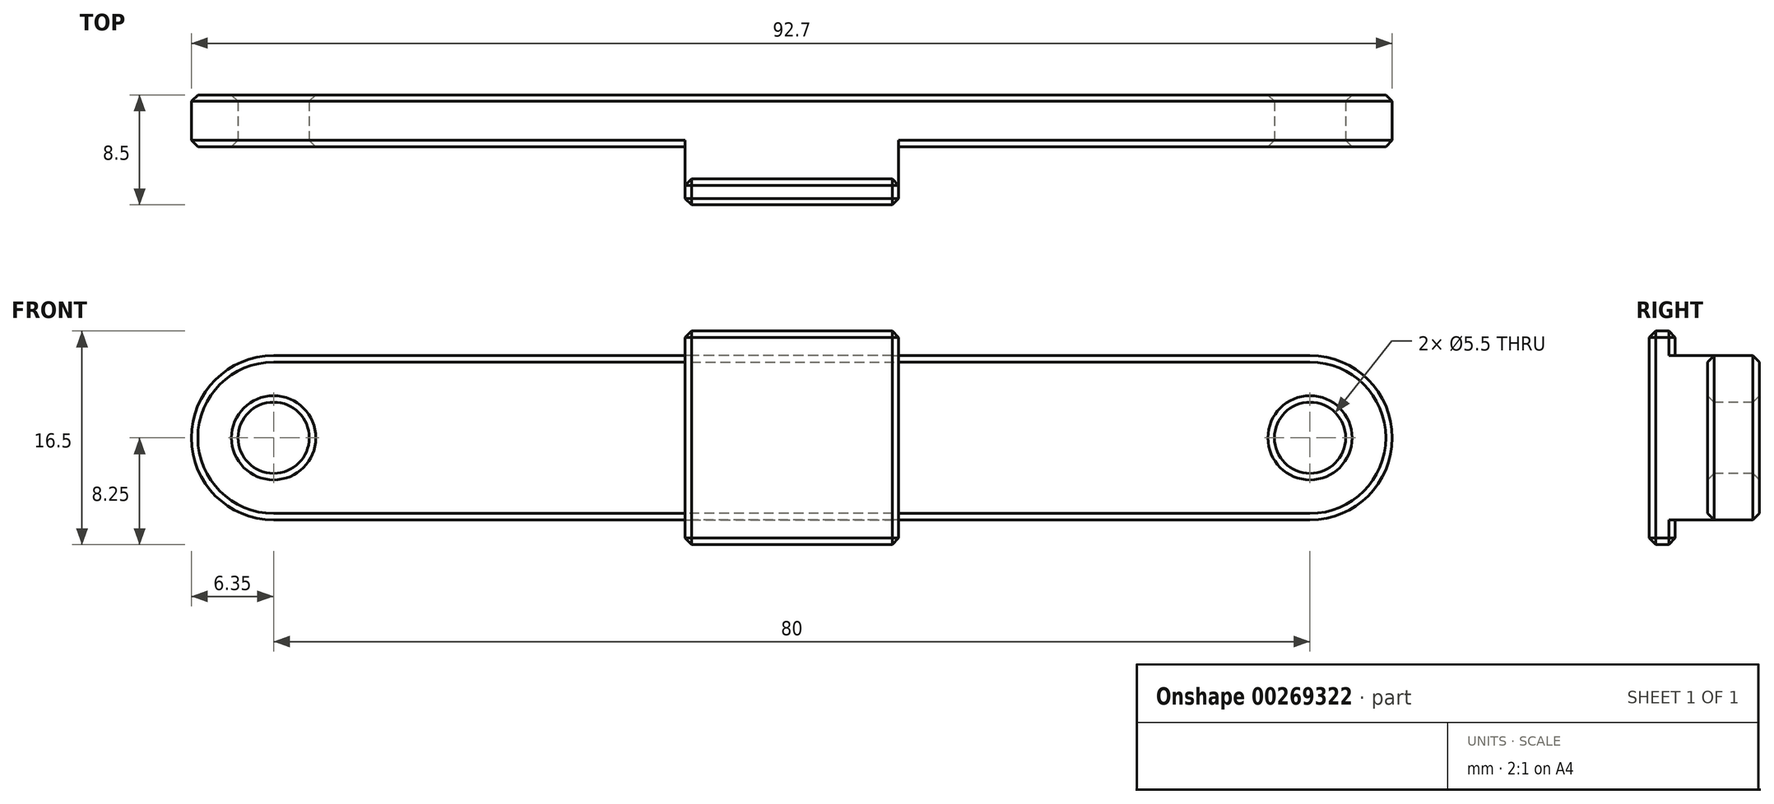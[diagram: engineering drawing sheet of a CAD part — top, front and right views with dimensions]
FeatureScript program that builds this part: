
annotation { "Feature Type Name" : "Feature", "Feature Type Description" : "" }
export const myFeature = defineFeature(function(context is Context, id is Id, definition is map)
    precondition{}
    {
        {
            var Q0;
            Q0=qCreatedBy(makeId("Front.planeOp"),FACE);
            var sketch = newSketch(context, id + "F0", { "sketchPlane" : qUnion([Q0])});
            skLineSegment(sketch, "E0.bottom", {"start": v(40, 6.35) * mm, "end": v(-40, 6.35) * mm});
            skLineSegment(sketch, "E0.top", {"start": v(40, -6.35) * mm, "end": v(-40, -6.35) * mm});
            skPoint(sketch, "E0.middle", {"position": v(0, 0) * mm});
            skArc(sketch, "E1", {"start": v(-40, 6.35) * mm, "mid": v(-46.35, 0) * mm, "end": v(-40, -6.35) * mm});
            skArc(sketch, "E2", {"start": v(40, -6.35) * mm, "mid": v(46.35, 0) * mm, "end": v(40, 6.35) * mm});
            skCircle(sketch, "E3", {"center": v(-40, 0) * mm, "radius": 2.75 * mm});
            skCircle(sketch, "E4", {"center": v(40, 0) * mm, "radius": 2.75 * mm});
            skSolve(sketch);
        }
        {
            var Q0;
            Q0=qSketchRegion(id+"F0",true);
            extrude(context, id + "F1", {"entities" : qUnion([Q0]), "oppositeDirection" : true, "depth" : 4 * mm});
        }
        {
            var Q0;
            Q0=qCreatedBy(makeId("Front.planeOp"),FACE);
            var sketch = newSketch(context, id + "F2", { "sketchPlane" : qUnion([Q0])});
            skLineSegment(sketch, "E5.bottom", {"start": v(8.25, 8.25) * mm, "end": v(-8.25, 8.25) * mm});
            skLineSegment(sketch, "E5.top", {"start": v(8.25, -8.25) * mm, "end": v(-8.25, -8.25) * mm});
            skLineSegment(sketch, "E5.left", {"start": v(8.25, 8.25) * mm, "end": v(8.25, -8.25) * mm});
            skLineSegment(sketch, "E5.right", {"start": v(-8.25, 8.25) * mm, "end": v(-8.25, -8.25) * mm});
            skPoint(sketch, "E5.middle", {"position": v(0, 0) * mm});
            skSolve(sketch);
        }
        {
            var Q0;
            Q0=makeQuery(id+"F2.imprint","IMPRINT",FACE,{"disambiguationData":[TD([[makeQuery(id+"F2.imprint","IMPRINT",EDGE,{"derivedFrom":sQuery(id+"F2.wireOp",EDGE,"E5.bottom")}),1.0]])]});
            extrude(context, id + "F3", {"entities" : qUnion([Q0]), "operationType" : NewBodyOperationType.ADD, "depth" : 4.5 * mm});
        }
        {
            var Q0;
            Q0=makeQuery(id+"F1.opExtrude","CAP_FACE",FACE,{"disambiguationData":[OSD([sQuery(id+"F0.wireOp",EDGE,"E0.bottom"),sQuery(id+"F0.wireOp",EDGE,"E0.top"),sQuery(id+"F0.wireOp",EDGE,"E1"),sQuery(id+"F0.wireOp",EDGE,"E2"),sQuery(id+"F0.wireOp",EDGE,"E3"),sQuery(id+"F0.wireOp",EDGE,"E4")])],"isStart":true});
            var sketch = newSketch(context, id + "F4", { "sketchPlane" : qUnion([Q0])});
            skLineSegment(sketch, "E6.bottom", {"start": v(8.25, -6.35) * mm, "end": v(-8.25, -6.35) * mm});
            skLineSegment(sketch, "E6.top", {"start": v(8.25, 6.35) * mm, "end": v(-8.25, 6.35) * mm});
            skLineSegment(sketch, "E6.left", {"start": v(8.25, -6.35) * mm, "end": v(8.25, 6.35) * mm});
            skLineSegment(sketch, "E6.right", {"start": v(-8.25, -6.35) * mm, "end": v(-8.25, 6.35) * mm});
            skPoint(sketch, "E6.middle", {"position": v(0, 0) * mm});
            skLineSegment(sketch, "E7.0", {"start": v(13.25, 11.35) * mm, "end": v(-13.25, 11.35) * mm});
            skLineSegment(sketch, "E7.1", {"start": v(13.25, -11.35) * mm, "end": v(13.25, 11.35) * mm});
            skLineSegment(sketch, "E7.2", {"start": v(13.25, -11.35) * mm, "end": v(-13.25, -11.35) * mm});
            skLineSegment(sketch, "E7.3", {"start": v(-13.25, -11.35) * mm, "end": v(-13.25, 11.35) * mm});
            skSolve(sketch);
        }
        {
            var Q0;
            Q0=qSketchRegion(id+"F4",true);
            extrude(context, id + "F5", {"entities" : qUnion([Q0]), "operationType" : NewBodyOperationType.REMOVE, "depth" : 2.5 * mm});
        }
        {
            var Q0;
            {var subQ0=sQuery(id+"F0.wireOp",EDGE,"E3");var subQ1=sQuery(id+"F0.wireOp",EDGE,"E1");var subQ3=sQuery(id+"F0.wireOp",EDGE,"E0.top");var subQ4=sQuery(id+"F0.wireOp",EDGE,"E0.bottom");Q0=makeQuery(id+"F3.boolean.opBoolean","SPLIT",FACE,{"disambiguationData":[TD([makeQuery(id+"F1.opExtrude","SWEPT_FACE",FACE,{"disambiguationData":[OSD([subQ1])]})])],"derivedFrom":makeQuery(id+"F1.opExtrude","CAP_FACE",FACE,{"disambiguationData":[OSD([subQ4,subQ3,subQ1,sQuery(id+"F0.wireOp",EDGE,"E2"),subQ0,sQuery(id+"F0.wireOp",EDGE,"E4")])],"isStart":true})});}
            var sketch = newSketch(context, id + "F6", { "sketchPlane" : qUnion([Q0])});
            skCircle(sketch, "E8", {"center": v(-25, 0) * mm, "radius": 2.75 * mm});
            skCircle(sketch, "E9", {"center": v(25, 0) * mm, "radius": 2.75 * mm});
            skSolve(sketch);
        }
        {
            var Q0;
            Q0=makeQuery(id+"F3.opExtrude","CAP_FACE",FACE,{"disambiguationData":[OSD([sQuery(id+"F2.wireOp",EDGE,"E5.bottom"),sQuery(id+"F2.wireOp",EDGE,"E5.top"),sQuery(id+"F2.wireOp",EDGE,"E5.left"),sQuery(id+"F2.wireOp",EDGE,"E5.right")])],"isStart":false});
            var Q1;
            Q1=makeQuery(id+"F3.opExtrude","SWEPT_EDGE",EDGE,{"disambiguationData":[OSD([sQuery(id+"F2.wireOp",EDGE,"E5.bottom"),sQuery(id+"F2.wireOp",EDGE,"E5.left")])]});
            var Q2;
            Q2=makeQuery(id+"F3.opExtrude","SWEPT_EDGE",EDGE,{"disambiguationData":[OSD([sQuery(id+"F2.wireOp",EDGE,"E5.bottom"),sQuery(id+"F2.wireOp",EDGE,"E5.right")])]});
            var Q3;
            Q3=makeQuery(id+"F3.opExtrude","SWEPT_EDGE",EDGE,{"disambiguationData":[OSD([sQuery(id+"F2.wireOp",EDGE,"E5.top"),sQuery(id+"F2.wireOp",EDGE,"E5.right")])]});
            var Q4;
            Q4=makeQuery(id+"F3.opExtrude","SWEPT_EDGE",EDGE,{"disambiguationData":[OSD([sQuery(id+"F2.wireOp",EDGE,"E5.top"),sQuery(id+"F2.wireOp",EDGE,"E5.left")])]});
            var Q5;
            Q5=makeQuery(id+"F1.opExtrude","CAP_FACE",FACE,{"disambiguationData":[OSD([sQuery(id+"F0.wireOp",EDGE,"E0.bottom"),sQuery(id+"F0.wireOp",EDGE,"E0.top"),sQuery(id+"F0.wireOp",EDGE,"E1"),sQuery(id+"F0.wireOp",EDGE,"E2"),sQuery(id+"F0.wireOp",EDGE,"E3"),sQuery(id+"F0.wireOp",EDGE,"E4")])],"isStart":false});
            var Q6;
            Q6=makeQuery(id+"F5.boolean.opBoolean","INTERSECT",EDGE,{"derivedFrom":[makeQuery(id+"F3.opExtrude","SWEPT_FACE",FACE,{"disambiguationData":[OSD([sQuery(id+"F2.wireOp",EDGE,"E5.bottom")])]}),makeQuery(id+"F5.opExtrude","CAP_FACE",FACE,{"disambiguationData":[OSD([sQuery(id+"F4.wireOp",EDGE,"E6.bottom"),sQuery(id+"F4.wireOp",EDGE,"E6.top"),sQuery(id+"F4.wireOp",EDGE,"E6.left"),sQuery(id+"F4.wireOp",EDGE,"E6.right"),sQuery(id+"F4.wireOp",EDGE,"E7.0"),sQuery(id+"F4.wireOp",EDGE,"E7.1"),sQuery(id+"F4.wireOp",EDGE,"E7.2"),sQuery(id+"F4.wireOp",EDGE,"E7.3")])],"isStart":false})]});
            var Q7;
            Q7=makeQuery(id+"F5.boolean.opBoolean","INTERSECT",EDGE,{"derivedFrom":[makeQuery(id+"F3.opExtrude","SWEPT_FACE",FACE,{"disambiguationData":[OSD([sQuery(id+"F2.wireOp",EDGE,"E5.left")])]}),makeQuery(id+"F5.opExtrude","CAP_FACE",FACE,{"disambiguationData":[OSD([sQuery(id+"F4.wireOp",EDGE,"E6.bottom"),sQuery(id+"F4.wireOp",EDGE,"E6.top"),sQuery(id+"F4.wireOp",EDGE,"E6.left"),sQuery(id+"F4.wireOp",EDGE,"E6.right"),sQuery(id+"F4.wireOp",EDGE,"E7.0"),sQuery(id+"F4.wireOp",EDGE,"E7.1"),sQuery(id+"F4.wireOp",EDGE,"E7.2"),sQuery(id+"F4.wireOp",EDGE,"E7.3")])],"isStart":false})]});
            var Q8;
            Q8=makeQuery(id+"F5.boolean.opBoolean","INTERSECT",EDGE,{"derivedFrom":[makeQuery(id+"F3.opExtrude","SWEPT_FACE",FACE,{"disambiguationData":[OSD([sQuery(id+"F2.wireOp",EDGE,"E5.right")])]}),makeQuery(id+"F5.opExtrude","CAP_FACE",FACE,{"disambiguationData":[OSD([sQuery(id+"F4.wireOp",EDGE,"E6.bottom"),sQuery(id+"F4.wireOp",EDGE,"E6.top"),sQuery(id+"F4.wireOp",EDGE,"E6.left"),sQuery(id+"F4.wireOp",EDGE,"E6.right"),sQuery(id+"F4.wireOp",EDGE,"E7.0"),sQuery(id+"F4.wireOp",EDGE,"E7.1"),sQuery(id+"F4.wireOp",EDGE,"E7.2"),sQuery(id+"F4.wireOp",EDGE,"E7.3")])],"isStart":false})]});
            var Q9;
            Q9=makeQuery(id+"F5.boolean.opBoolean","INTERSECT",EDGE,{"derivedFrom":[makeQuery(id+"F3.opExtrude","SWEPT_FACE",FACE,{"disambiguationData":[OSD([sQuery(id+"F2.wireOp",EDGE,"E5.top")])]}),makeQuery(id+"F5.opExtrude","CAP_FACE",FACE,{"disambiguationData":[OSD([sQuery(id+"F4.wireOp",EDGE,"E6.bottom"),sQuery(id+"F4.wireOp",EDGE,"E6.top"),sQuery(id+"F4.wireOp",EDGE,"E6.left"),sQuery(id+"F4.wireOp",EDGE,"E6.right"),sQuery(id+"F4.wireOp",EDGE,"E7.0"),sQuery(id+"F4.wireOp",EDGE,"E7.1"),sQuery(id+"F4.wireOp",EDGE,"E7.2"),sQuery(id+"F4.wireOp",EDGE,"E7.3")])],"isStart":false})]});
            var Q10;
            {var subQ0=sQuery(id+"F2.wireOp",EDGE,"E5.left");var subQ1=makeQuery(id+"F3.opExtrude","SWEPT_FACE",FACE,{"disambiguationData":[OSD([subQ0])]});var subQ2=sQuery(id+"F2.wireOp",EDGE,"E5.right");var subQ3=makeQuery(id+"F3.opExtrude","CAP_FACE",FACE,{"disambiguationData":[OSD([sQuery(id+"F2.wireOp",EDGE,"E5.bottom"),sQuery(id+"F2.wireOp",EDGE,"E5.top"),subQ0,subQ2])],"isStart":true});var subQ4=sQuery(id+"F0.wireOp",EDGE,"E2");var subQ5=sQuery(id+"F0.wireOp",EDGE,"E0.bottom");var subQ6=makeQuery(id+"F1.opExtrude","CAP_FACE",FACE,{"disambiguationData":[OSD([subQ5,sQuery(id+"F0.wireOp",EDGE,"E0.top"),sQuery(id+"F0.wireOp",EDGE,"E1"),subQ4,sQuery(id+"F0.wireOp",EDGE,"E3"),sQuery(id+"F0.wireOp",EDGE,"E4")])],"isStart":true});var subQ7=makeQuery(id+"F1.opExtrude","SWEPT_FACE",FACE,{"disambiguationData":[OSD([subQ5])]});var subQ8=makeQuery(id+"F1.opExtrude","CAP_EDGE",EDGE,{"disambiguationData":[OSD([subQ5])],"isStart":true});Q10=makeQuery(id+"F5.boolean.opBoolean","MERGE",EDGE,{"derivedFrom":[makeQuery(id+"F3.boolean.opBoolean","SPLIT",EDGE,{"disambiguationData":[TD([subQ7,subQ6,makeQuery(id+"F1.opExtrude","SWEPT_FACE",FACE,{"disambiguationData":[OSD([subQ4])]}),subQ3,subQ1])],"derivedFrom":subQ8}),makeQuery(id+"F3.boolean.opBoolean","SPLIT",EDGE,{"disambiguationData":[TD([subQ7,subQ6,subQ3,subQ1,makeQuery(id+"F3.opExtrude","SWEPT_FACE",FACE,{"disambiguationData":[OSD([subQ2])]})])],"derivedFrom":subQ8})]});}
            var Q11;
            Q11=makeQuery(id+"F1.opExtrude","CAP_EDGE",EDGE,{"disambiguationData":[OSD([sQuery(id+"F0.wireOp",EDGE,"E4")])],"isStart":true});
            var Q12;
            Q12=makeQuery(id+"F5.boolean.opBoolean","COPY",EDGE,{"derivedFrom":makeQuery(id+"F5.opExtrude","SWEPT_EDGE",EDGE,{"disambiguationData":[OSD([sQuery(id+"F4.wireOp",EDGE,"E6.top"),sQuery(id+"F4.wireOp",EDGE,"E6.left")])]})});
            var Q13;
            Q13=makeQuery(id+"F5.boolean.opBoolean","COPY",EDGE,{"derivedFrom":makeQuery(id+"F5.opExtrude","SWEPT_EDGE",EDGE,{"disambiguationData":[OSD([sQuery(id+"F4.wireOp",EDGE,"E6.bottom"),sQuery(id+"F4.wireOp",EDGE,"E6.left")])]})});
            var Q14;
            Q14=makeQuery(id+"F5.boolean.opBoolean","COPY",EDGE,{"derivedFrom":makeQuery(id+"F5.opExtrude","SWEPT_EDGE",EDGE,{"disambiguationData":[OSD([sQuery(id+"F4.wireOp",EDGE,"E6.top"),sQuery(id+"F4.wireOp",EDGE,"E6.right")])]})});
            var Q15;
            Q15=makeQuery(id+"F5.boolean.opBoolean","COPY",EDGE,{"derivedFrom":makeQuery(id+"F5.opExtrude","SWEPT_EDGE",EDGE,{"disambiguationData":[OSD([sQuery(id+"F4.wireOp",EDGE,"E6.bottom"),sQuery(id+"F4.wireOp",EDGE,"E6.right")])]})});
            var Q16;
            {var subQ0=sQuery(id+"F2.wireOp",EDGE,"E5.left");var subQ1=sQuery(id+"F0.wireOp",EDGE,"E0.top");var subQ2=makeQuery(id+"F1.opExtrude","SWEPT_FACE",FACE,{"disambiguationData":[OSD([subQ1])]});var subQ3=sQuery(id+"F2.wireOp",EDGE,"E5.right");var subQ4=makeQuery(id+"F3.opExtrude","CAP_FACE",FACE,{"disambiguationData":[OSD([sQuery(id+"F2.wireOp",EDGE,"E5.bottom"),sQuery(id+"F2.wireOp",EDGE,"E5.top"),subQ0,subQ3])],"isStart":true});var subQ5=sQuery(id+"F0.wireOp",EDGE,"E1");var subQ6=makeQuery(id+"F1.opExtrude","CAP_FACE",FACE,{"disambiguationData":[OSD([sQuery(id+"F0.wireOp",EDGE,"E0.bottom"),subQ1,subQ5,sQuery(id+"F0.wireOp",EDGE,"E2"),sQuery(id+"F0.wireOp",EDGE,"E3"),sQuery(id+"F0.wireOp",EDGE,"E4")])],"isStart":true});var subQ7=makeQuery(id+"F3.opExtrude","SWEPT_FACE",FACE,{"disambiguationData":[OSD([subQ3])]});var subQ8=makeQuery(id+"F1.opExtrude","CAP_EDGE",EDGE,{"disambiguationData":[OSD([subQ1])],"isStart":true});Q16=makeQuery(id+"F5.boolean.opBoolean","MERGE",EDGE,{"derivedFrom":[makeQuery(id+"F3.boolean.opBoolean","SPLIT",EDGE,{"disambiguationData":[TD([subQ6,subQ2,makeQuery(id+"F1.opExtrude","SWEPT_FACE",FACE,{"disambiguationData":[OSD([subQ5])]}),subQ4,subQ7])],"derivedFrom":subQ8}),makeQuery(id+"F3.boolean.opBoolean","SPLIT",EDGE,{"disambiguationData":[TD([subQ6,subQ2,subQ4,makeQuery(id+"F3.opExtrude","SWEPT_FACE",FACE,{"disambiguationData":[OSD([subQ0])]}),subQ7])],"derivedFrom":subQ8})]});}
            var Q17;
            Q17=makeQuery(id+"F1.opExtrude","CAP_EDGE",EDGE,{"disambiguationData":[OSD([sQuery(id+"F0.wireOp",EDGE,"E3")])],"isStart":true});
            var Q18;
            Q18=makeQuery(id+"FtL2NpPsK7YUmwO_2.boolean.opBoolean","COPY",EDGE,{"derivedFrom":makeQuery(id+"FtL2NpPsK7YUmwO_2.opExtrude","CAP_EDGE",EDGE,{"disambiguationData":[OSD([sQuery(id+"F6.wireOp",EDGE,"E8")])],"isStart":true})});
            var Q19;
            Q19=makeQuery(id+"FtL2NpPsK7YUmwO_2.boolean.opBoolean","COPY",EDGE,{"derivedFrom":makeQuery(id+"FtL2NpPsK7YUmwO_2.opExtrude","CAP_EDGE",EDGE,{"disambiguationData":[OSD([sQuery(id+"F6.wireOp",EDGE,"E9")])],"isStart":true})});
            chamfer(context, id + "F7", {"entities" : qUnion([Q0, Q1, Q2, Q3, Q4, Q5, Q6, Q7, Q8, Q9, Q10, Q11, Q12, Q13, Q14, Q15, Q16, Q17, Q18, Q19]), "width" : 0.5 * mm, "tangentPropagation" : true});
        }
    });
